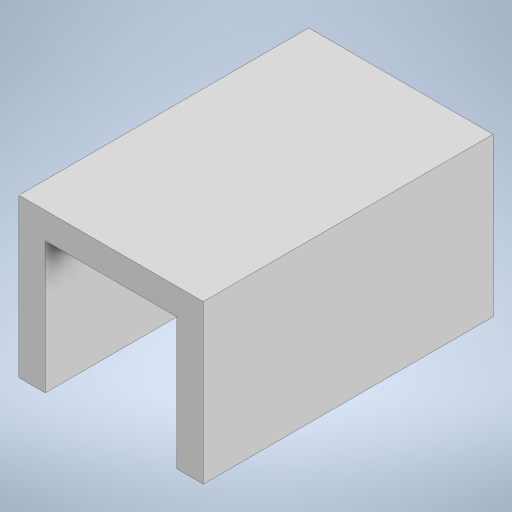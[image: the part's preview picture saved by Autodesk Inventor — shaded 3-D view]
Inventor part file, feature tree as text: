
AUTODESK INVENTOR PART (.ipt)
format: ipt  version: 2023 (Build 270158000, 158)  size: 184,832 bytes
history: native  units: in
note: dims shown in document units (in); Inventor stores cm internally (conversion verified against a paired STEP export)
features: sketch x6, extrude x3
ambient origin geometry x8: Origin, YZ Plane, XZ Plane, XY Plane, X Axis, Y Axis, Z Axis, Center Point
bodies: Solid1 (feature_tree)
feature tree (9):
  extrude  "Extrusion1"  Depth=0.4724in
  extrude  "Extrusion2"  Depth=0.3937in
  sketch  "Sketch8"  dims[d5=0.7874in d6=0.7874in d7=0.0in]
  sketch  "Sketch9"  dims[d27=0.1969in]
  sketch  "Sketch11"  dims[d28=0.3937in d29=0.0in]
  extrude  "Extrusion9"  Depth=0.7874in TaperAngle=0.0deg
  sketch  "Sketch1"  dims[d0=0.5512in d1=0.4724in]
  sketch  "Sketch2"  dims[d2=0.8661in d3=0.0in d4=0.3937in]
  sketch  "Sketch13"
